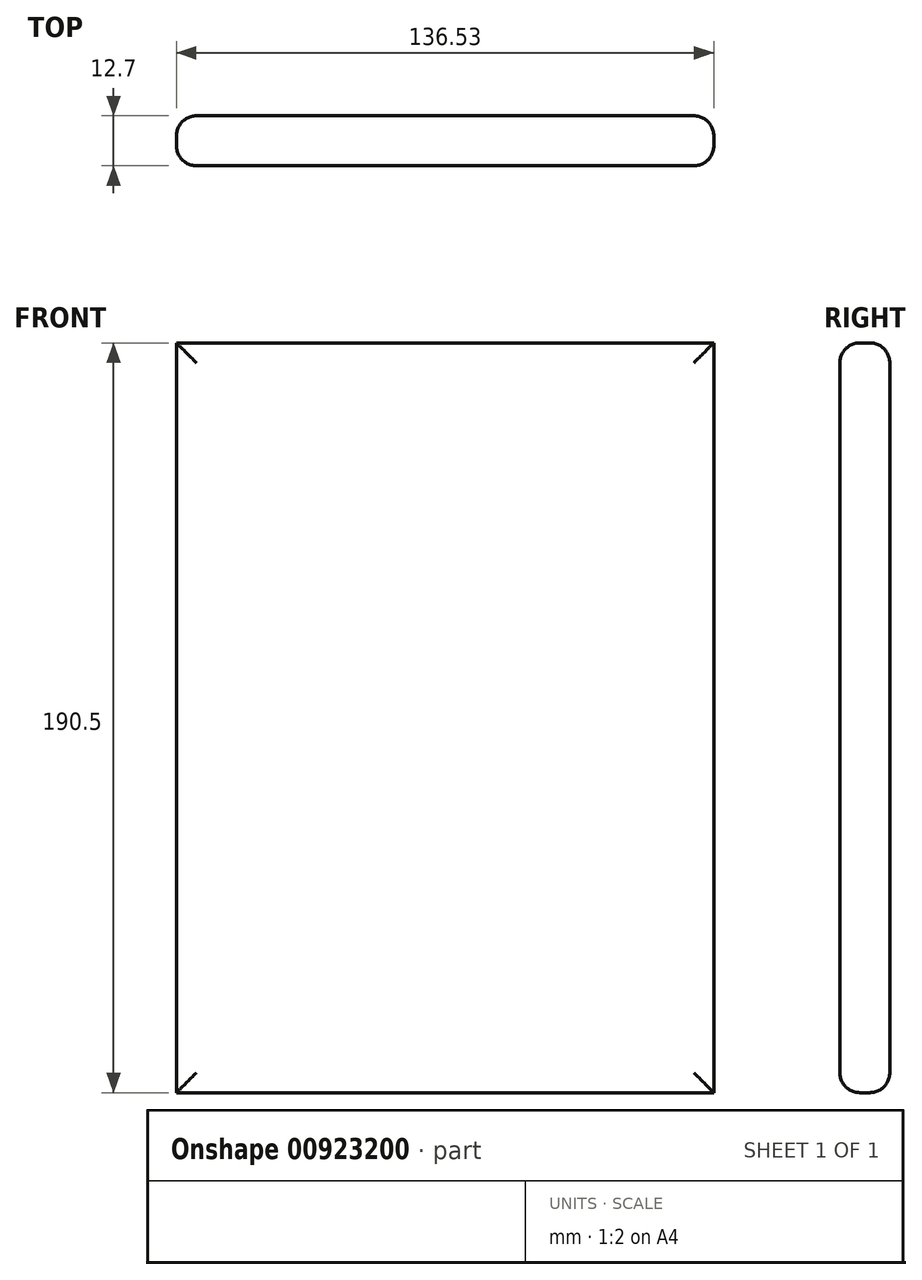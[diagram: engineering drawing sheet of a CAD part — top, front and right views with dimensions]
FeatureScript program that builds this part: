
annotation { "Feature Type Name" : "Feature", "Feature Type Description" : "" }
export const myFeature = defineFeature(function(context is Context, id is Id, definition is map)
    precondition{}
    {
        {
            var Q0;
            Q0=qCreatedBy(makeId("Front.planeOp"),FACE);
            var sketch = newSketch(context, id + "F0", { "sketchPlane" : qUnion([Q0])});
            skLineSegment(sketch, "E0.bottom", {"start": v(0, 0) * mm, "end": v(136.53, 0) * mm});
            skLineSegment(sketch, "E0.top", {"start": v(0, 190.5) * mm, "end": v(136.52, 190.5) * mm});
            skLineSegment(sketch, "E0.left", {"start": v(0, 0) * mm, "end": v(0, 190.5) * mm});
            skLineSegment(sketch, "E0.right", {"start": v(136.53, 0) * mm, "end": v(136.53, 190.5) * mm});
            skSolve(sketch);
        }
        {
            var Q0;
            Q0 = qSketchRegion(id + "F0", true);
            extrude(context, id + "F1", {"entities" : qUnion([Q0]), "depth" : 12.7 * mm, "offsetDistance" : 25.4 * mm});
        }
        {
            var Q0;
            Q0=makeQuery(id+"F1.opExtrude","CAP_FACE",FACE,{"disambiguationData":[OSD([sQuery(id+"F0.wireOp",EDGE,"E0.bottom"),sQuery(id+"F0.wireOp",EDGE,"E0.top"),sQuery(id+"F0.wireOp",EDGE,"E0.left"),sQuery(id+"F0.wireOp",EDGE,"E0.right")])],"isStart":false});
            var Q1;
            Q1=makeQuery(id+"F1.opExtrude","CAP_FACE",FACE,{"disambiguationData":[OSD([sQuery(id+"F0.wireOp",EDGE,"E0.bottom"),sQuery(id+"F0.wireOp",EDGE,"E0.top"),sQuery(id+"F0.wireOp",EDGE,"E0.left"),sQuery(id+"F0.wireOp",EDGE,"E0.right")])],"isStart":true});
            fillet(context, id + "F2", {"entities" : qUnion([Q0, Q1]), "radius" : 5.08 * mm, "tangentPropagation" : true, "allowEdgeOverflow" : false});
        }
    });
